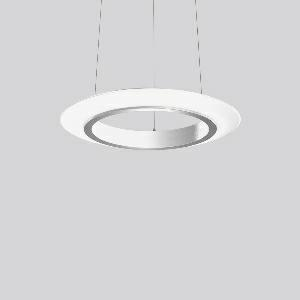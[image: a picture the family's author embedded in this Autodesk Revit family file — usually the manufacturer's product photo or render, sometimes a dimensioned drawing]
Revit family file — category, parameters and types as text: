
# Revit family: ring_of_fire_p_311669_004_730_ea63
name_source: partatom
category: Lighting Fixtures
units: mm (PartAtom-declared; Revit-internal decimal feet)

## family parameters
Cut with Voids When Loaded = No
Host = Face
Light Source = No
Part Type = Normal
Room Calculation Point = No
Round Connector Dimension = Use Diameter
Shared = No

## types (1)
- RING OF FIRE P (1 x LED Modul 830, 2800 lm, 3000)
    Apparent Load = 28 VA
    CIE Flux Codes = 43 72 89 54 100
    Color Rendering = 80
    Color Temperature = 3000
    Default Elevation = 1800 mm
    Description = Series: RING OF FIRE
A uniquely shaped pendant luminaire with elliptical glass. Supporting ring made of anodised aluminium. Canopy aluminium anodised. Opal glass: mouth-blown, satin finish. Suitable for pendant. 3-point steel cable suspension, steplessly adjustable. Special lengths available on request. For pendant lengths of up to 2 m, power is supplied through a suspension cable. For pendant lengths of 2 m and more, power must be supplied through a separate cable. Converter integrated in the canopy. With Casambi smart+free Bluetooth control for wireless network and operation using Android / iOS devices, free app available for download. 
Colour: anodised aluminium
Diameter: 495 mm
Height: 55 mm
Suspension length: 500-1200 mm
Lamp: LED
Socket: without socket
Colour temperature: 3000K
Colour rendering index (CRI): 80
System power: 28 W
Rated luminous flux: 2800 lm
Luminous efficiency: 100 lm/W
Control gear: Dimmable Bluetooth converter
Protection class: I
Type of protection: IP 20
    Height = 55 mm
    Lamp = 1 x LED Modul 830
    Lamp Light Flux = 2800 lm
    Lamp count = 1
    Length = 495 mm
    Lifetime = 50000 h
    Luminous efficacy = 100 lm/W
    Manufacturer = RZB
    ModVariant = No
    Model = 311669.004.730
    Mounting Place = Ceiling
    Mounting Type = Pendant
    Number of Poles = 1
    OnlyDefault = Yes
    Power Factor = 1
    Product Name = RING OF FIRE P
    Product group = Pendant luminaires
    ProductGroupID = 902
    Protection Class = Protection class I
    Protection Degree = IP 20
    RLX_Detail_Level = 1
    RLX_Emergency_Light_Flux = 0 lm
    RLX_Emergency_Type = 0
    RLX_Emergency_Type_DB = No
    RlxData = <blob elided: 38037 chars, md5=5e976cc0>
    Socket = socket
    Standby Power = 0 W
    System Light Flux = 2800 lm
    System Power = 28 W
    Type Comments = Product without accessories
    Type Image = 311669.004.jpg
    URL = http://relux.com
    VarID = ---
    Voltage = 230 V
    Voltage Range = 220-240 V
    Weight = 0.00 kg
    Width = 0 mm  [stored 0 ft]

note: [stored X ft] marks values corroborated as IEEE doubles in the binary element streams (Revit-internal decimal feet)

## geometry (parser evidence)
native form markers: Blend x4, Sweep x13
no freeform markers — native parametric forms only
